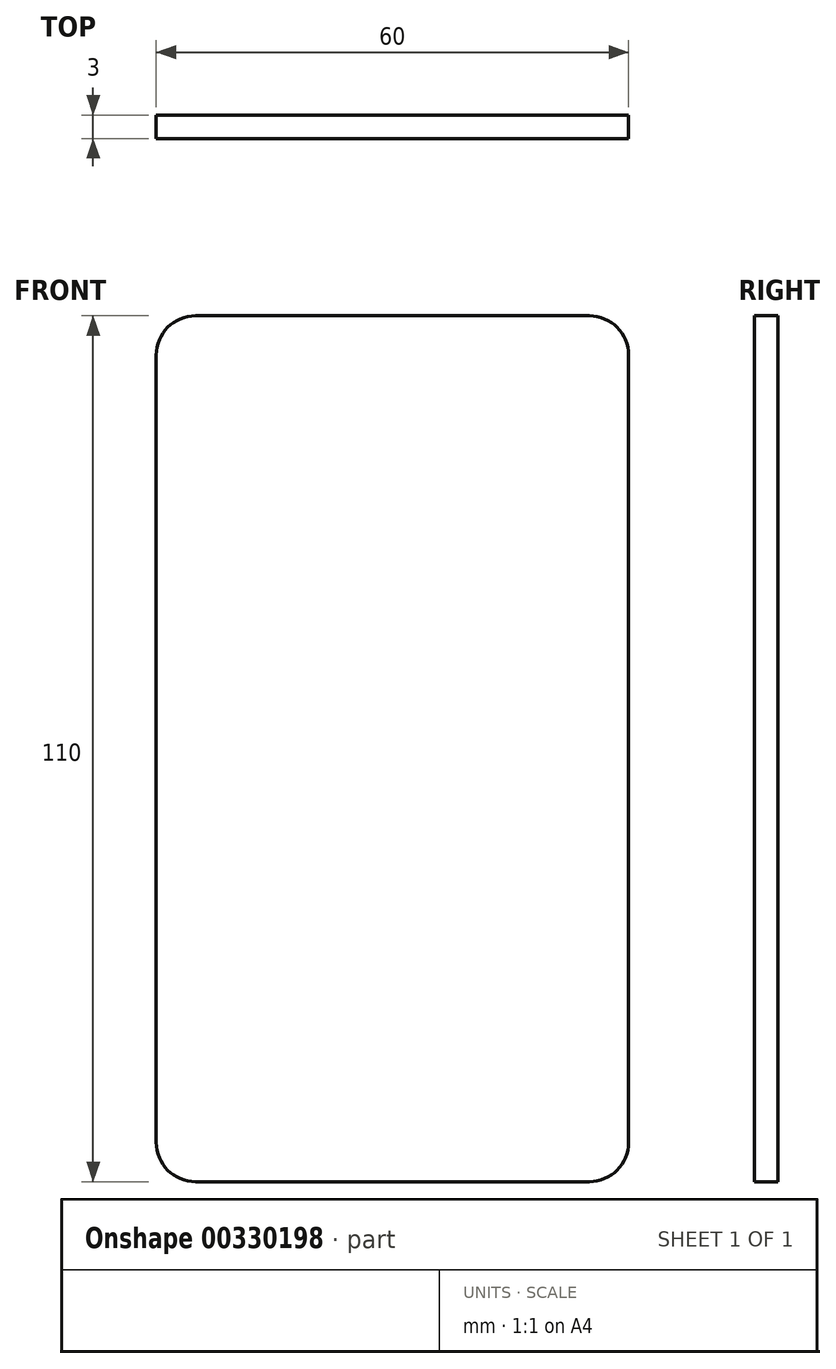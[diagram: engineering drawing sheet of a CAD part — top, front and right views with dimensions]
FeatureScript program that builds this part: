
annotation { "Feature Type Name" : "Feature", "Feature Type Description" : "" }
export const myFeature = defineFeature(function(context is Context, id is Id, definition is map)
    precondition{}
    {
        {
            var Q0;
            Q0=qCreatedBy(makeId("Front.planeOp"),FACE);
            var sketch = newSketch(context, id + "F0", { "sketchPlane" : qUnion([Q0])});
            skLineSegment(sketch, "E0.bottom", {"start": v(11.27, 20.04) * mm, "end": v(-48.73, 20.04) * mm});
            skLineSegment(sketch, "E0.top", {"start": v(11.27, -89.96) * mm, "end": v(-48.73, -89.96) * mm});
            skLineSegment(sketch, "E0.left", {"start": v(11.27, 20.04) * mm, "end": v(11.27, -89.96) * mm});
            skLineSegment(sketch, "E0.right", {"start": v(-48.73, 20.04) * mm, "end": v(-48.73, -89.96) * mm});
            skPoint(sketch, "E0.middle", {"position": v(-18.73, -34.96) * mm});
            skSolve(sketch);
        }
        {
            var Q0;
            Q0=makeQuery(id+"F0.imprint","IMPRINT",FACE,{"disambiguationData":[TD([[makeQuery(id+"F0.imprint","IMPRINT",EDGE,{"derivedFrom":sQuery(id+"F0.wireOp",EDGE,"E0.bottom")}),1.0]])]});
            extrude(context, id + "F1", {"entities" : qUnion([Q0]), "depth" : 3 * mm});
        }
        {
            var Q0;
            Q0=makeQuery(id+"F1.opExtrude","SWEPT_EDGE",EDGE,{"disambiguationData":[OSD([sQuery(id+"F0.wireOp",EDGE,"E0.top"),sQuery(id+"F0.wireOp",EDGE,"E0.right")])]});
            fillet(context, id + "F2", {"entities" : qUnion([Q0]), "radius" : 5 * mm, "tangentPropagation" : true, "allowEdgeOverflow" : false});
        }
        {
            var Q0;
            Q0=makeQuery(id+"F1.opExtrude","SWEPT_EDGE",EDGE,{"disambiguationData":[OSD([sQuery(id+"F0.wireOp",EDGE,"E0.top"),sQuery(id+"F0.wireOp",EDGE,"E0.left")])]});
            fillet(context, id + "F3", {"entities" : qUnion([Q0]), "radius" : 5 * mm, "tangentPropagation" : true, "allowEdgeOverflow" : false});
        }
        {
            var Q0;
            Q0=makeQuery(id+"F1.opExtrude","SWEPT_EDGE",EDGE,{"disambiguationData":[OSD([sQuery(id+"F0.wireOp",EDGE,"E0.bottom"),sQuery(id+"F0.wireOp",EDGE,"E0.right")])]});
            var Q1;
            Q1=makeQuery(id+"F1.opExtrude","SWEPT_EDGE",EDGE,{"disambiguationData":[OSD([sQuery(id+"F0.wireOp",EDGE,"E0.bottom"),sQuery(id+"F0.wireOp",EDGE,"E0.left")])]});
            fillet(context, id + "F4", {"entities" : qUnion([Q0, Q1]), "radius" : 5 * mm, "tangentPropagation" : true, "allowEdgeOverflow" : false});
        }
    });
